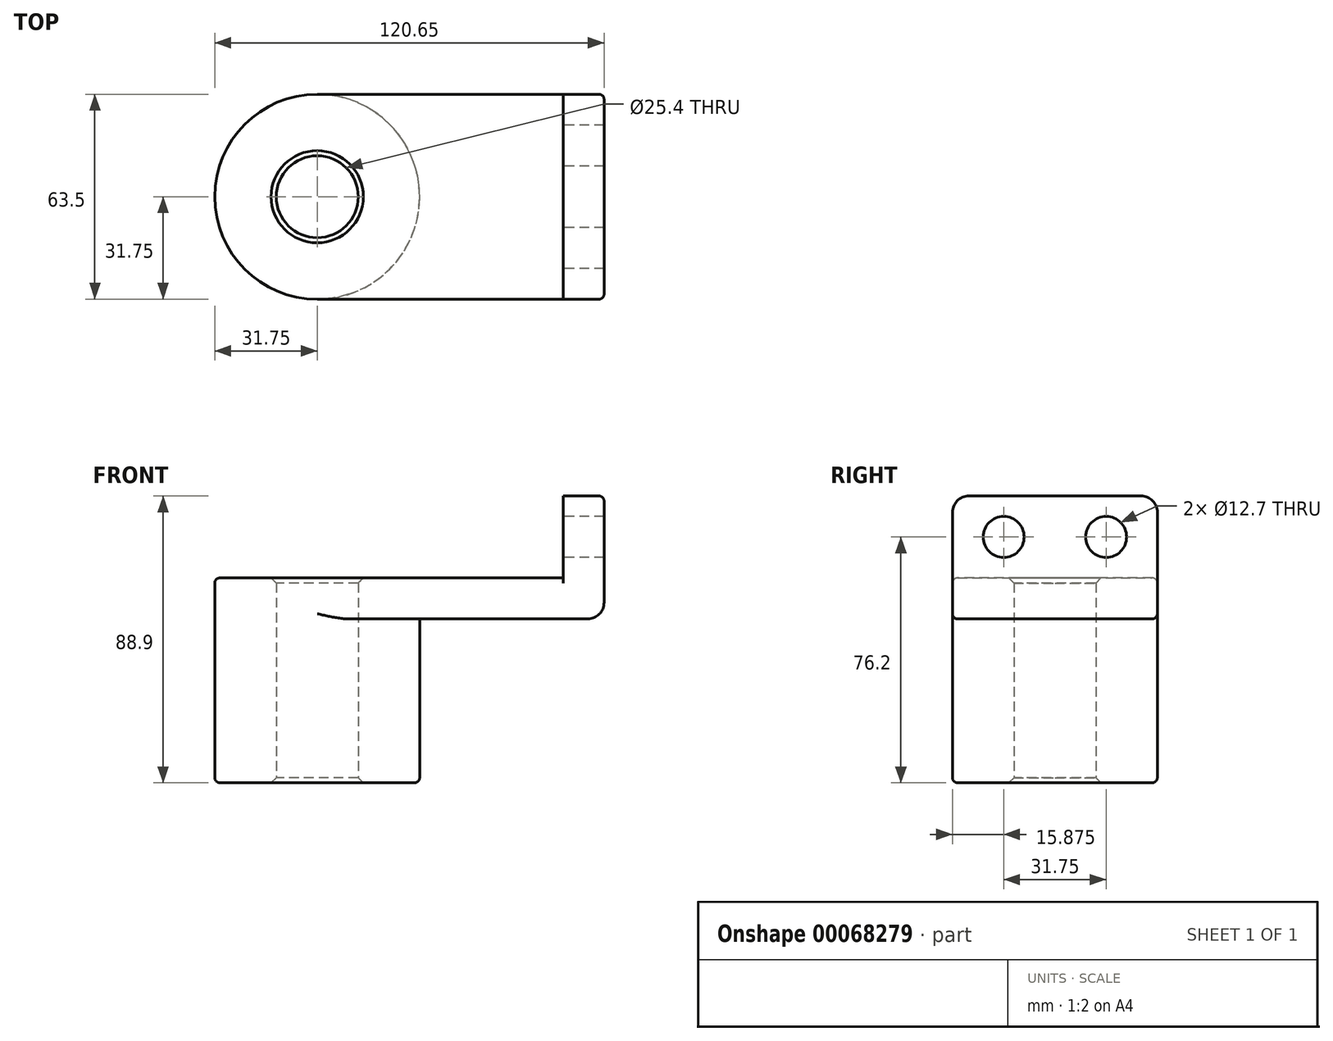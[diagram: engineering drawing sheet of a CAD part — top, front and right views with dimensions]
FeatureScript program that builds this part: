
annotation { "Feature Type Name" : "Feature", "Feature Type Description" : "" }
export const myFeature = defineFeature(function(context is Context, id is Id, definition is map)
    precondition{}
    {
        {
            var Q0;
            Q0=qCreatedBy(makeId("Top.planeOp"),FACE);
            var sketch = newSketch(context, id + "F0", { "sketchPlane" : qUnion([Q0])});
            skLineSegment(sketch, "E0.rect.bottom", {"start": v(38.1, -31.75) * mm, "end": v(-38.1, -31.75) * mm});
            skLineSegment(sketch, "E0.rect.top", {"start": v(38.1, 31.75) * mm, "end": v(-38.1, 31.75) * mm});
            skLineSegment(sketch, "E0.rect.left", {"start": v(38.1, -31.75) * mm, "end": v(38.1, 31.75) * mm});
            skLineSegment(sketch, "E0.rect.right", {"start": v(-38.1, -31.75) * mm, "end": v(-38.1, 31.75) * mm});
            skPoint(sketch, "E0.rect.middle", {"position": v(0, 0) * mm});
            skCircle(sketch, "E1", {"center": v(-38.1, 0) * mm, "radius": 31.75 * mm});
            skCircle(sketch, "E2", {"center": v(-38.1, 0) * mm, "radius": 12.7 * mm});
            skSolve(sketch);
        }
        {
            var Q0;
            {var subQ0=sQuery(id+"F0.wireOp",EDGE,"E0.rect.bottom");Q0=makeQuery(id+"F0.imprint","IMPRINT",FACE,{"disambiguationData":[TD([[makeQuery(id+"F0.imprint","IMPRINT",EDGE,{"derivedFrom":subQ0}),-1.0]])]});}
            var Q1;
            {var subQ1=sQuery(id+"F0.wireOp",EDGE,"E0.rect.right");var subQ3=sQuery(id+"F0.wireOp",EDGE,"E2");var subQ4=makeQuery(id+"F0.imprint","INTERSECT",VERTEX,{"disambiguationData":[OD(0.0)],"derivedFrom":[subQ1,subQ3]});Q1=makeQuery(id+"F0.imprint","IMPRINT",FACE,{"disambiguationData":[TD([[makeQuery(id+"F0.imprint","IMPRINT",EDGE,{"disambiguationData":[TD([[subQ4,-1.0]])],"derivedFrom":subQ3}),-1.0]])]});}
            var Q2;
            {var subQ1=sQuery(id+"F0.wireOp",EDGE,"E0.rect.right");var subQ3=sQuery(id+"F0.wireOp",EDGE,"E2");var subQ4=makeQuery(id+"F0.imprint","INTERSECT",VERTEX,{"disambiguationData":[OD(0.0)],"derivedFrom":[subQ1,subQ3]});Q2=makeQuery(id+"F0.imprint","IMPRINT",FACE,{"disambiguationData":[TD([[makeQuery(id+"F0.imprint","IMPRINT",EDGE,{"disambiguationData":[TD([[subQ4,1.0]])],"derivedFrom":subQ3}),-1.0]])]});}
            extrude(context, id + "F1", {"entities" : qUnion([Q0, Q1, Q2]), "depth" : 12.7 * mm});
        }
        {
            var Q0;
            {var subQ1=sQuery(id+"F0.wireOp",EDGE,"E0.rect.right");var subQ3=sQuery(id+"F0.wireOp",EDGE,"E2");var subQ4=makeQuery(id+"F0.imprint","INTERSECT",VERTEX,{"disambiguationData":[OD(0.0)],"derivedFrom":[subQ1,subQ3]});Q0=makeQuery(id+"F0.imprint","IMPRINT",FACE,{"disambiguationData":[TD([[makeQuery(id+"F0.imprint","IMPRINT",EDGE,{"disambiguationData":[TD([[subQ4,1.0]])],"derivedFrom":subQ3}),-1.0]])]});}
            var Q1;
            {var subQ1=sQuery(id+"F0.wireOp",EDGE,"E0.rect.right");var subQ3=sQuery(id+"F0.wireOp",EDGE,"E2");var subQ4=makeQuery(id+"F0.imprint","INTERSECT",VERTEX,{"disambiguationData":[OD(0.0)],"derivedFrom":[subQ1,subQ3]});Q1=makeQuery(id+"F0.imprint","IMPRINT",FACE,{"disambiguationData":[TD([[makeQuery(id+"F0.imprint","IMPRINT",EDGE,{"disambiguationData":[TD([[subQ4,-1.0]])],"derivedFrom":subQ3}),-1.0]])]});}
            extrude(context, id + "F2", {"entities" : qUnion([Q0, Q1]), "operationType" : NewBodyOperationType.ADD, "oppositeDirection" : true, "depth" : 50.8 * mm});
        }
        {
            var Q0;
            Q0=makeQuery(id+"F1.opExtrude","SWEPT_FACE",FACE,{"disambiguationData":[OSD([sQuery(id+"F0.wireOp",EDGE,"E0.rect.left")])]});
            var sketch = newSketch(context, id + "F3", { "sketchPlane" : qUnion([Q0])});
            skLineSegment(sketch, "E3.bottom", {"start": v(31.75, 0) * mm, "end": v(-31.75, 0) * mm});
            skLineSegment(sketch, "E3.top", {"start": v(31.75, 38.1) * mm, "end": v(-31.75, 38.1) * mm});
            skLineSegment(sketch, "E3.left", {"start": v(31.75, 0) * mm, "end": v(31.75, 38.1) * mm});
            skLineSegment(sketch, "E3.right", {"start": v(-31.75, 0) * mm, "end": v(-31.75, 38.1) * mm});
            skLineSegment(sketch, "E4", {"start": v(0, 12.7) * mm, "end": v(0, 38.1) * mm, "construction": true});
            skCircle(sketch, "E5", {"center": v(15.88, 25.4) * mm, "radius": 6.35 * mm});
            skCircle(sketch, "E6.MirrorC", {"center": v(-15.88, 25.4) * mm, "radius": 6.35 * mm});
            skSolve(sketch);
        }
        {
            var Q0;
            {var subQ2=sQuery(id+"F3.wireOp",EDGE,"E3.top");Q0=makeQuery(id+"F3.imprint","IMPRINT",FACE,{"disambiguationData":[TD([[makeQuery(id+"F3.imprint","IMPRINT",EDGE,{"derivedFrom":subQ2}),1.0]])]});}
            var Q1;
            {var subQ0=sQuery(id+"F3.wireOp",EDGE,"E3.bottom");Q1=makeQuery(id+"F3.imprint","IMPRINT",FACE,{"disambiguationData":[TD([[makeQuery(id+"F3.imprint","IMPRINT",EDGE,{"derivedFrom":subQ0}),1.0]])]});}
            extrude(context, id + "F4", {"entities" : qUnion([Q0, Q1]), "operationType" : NewBodyOperationType.ADD, "depth" : 12.7 * mm});
        }
        {
            var Q0;
            Q0=makeQuery(id+"F2.opExtrude","CAP_EDGE",EDGE,{"disambiguationData":[OSD([sQuery(id+"F0.wireOp",EDGE,"E1")])],"isStart":true});
            var Q1;
            Q1=makeQuery(id+"F4.opExtrude","SWEPT_EDGE",EDGE,{"disambiguationData":[OSD([sQuery(id+"F3.wireOp",EDGE,"E3.top"),sQuery(id+"F3.wireOp",EDGE,"E3.left")])]});
            var Q2;
            Q2=makeQuery(id+"F4.opExtrude","SWEPT_EDGE",EDGE,{"disambiguationData":[OSD([sQuery(id+"F3.wireOp",EDGE,"E3.top"),sQuery(id+"F3.wireOp",EDGE,"E3.right")])]});
            var Q3;
            Q3=makeQuery(id+"F4.opExtrude","CAP_EDGE",EDGE,{"disambiguationData":[OSD([sQuery(id+"F3.wireOp",EDGE,"E3.bottom")])],"isStart":false});
            var Q4;
            Q4=makeQuery(id+"F1.opExtrude","CAP_EDGE",EDGE,{"disambiguationData":[OSD([sQuery(id+"F0.wireOp",EDGE,"E0.rect.left")])],"isStart":false});
            fillet(context, id + "F5", {"entities" : qUnion([Q0, Q1, Q2, Q3, Q4]), "radius" : 5.08 * mm, "tangentPropagation" : true, "allowEdgeOverflow" : false});
        }
        {
            var Q0;
            Q0=makeQuery(id+"F1.opExtrude","CAP_EDGE",EDGE,{"disambiguationData":[OSD([sQuery(id+"F0.wireOp",EDGE,"E0.rect.bottom")])],"isStart":false});
            var Q1;
            Q1=makeQuery(id+"F4.boolean.opBoolean","MERGE",EDGE,{"derivedFrom":[makeQuery(id+"F1.opExtrude","CAP_EDGE",EDGE,{"disambiguationData":[OSD([sQuery(id+"F0.wireOp",EDGE,"E0.rect.bottom")])],"isStart":true}),makeQuery(id+"F4.opExtrude","SWEPT_EDGE",EDGE,{"disambiguationData":[OSD([sQuery(id+"F3.wireOp",EDGE,"E3.bottom"),sQuery(id+"F3.wireOp",EDGE,"E3.right")])]})]});
            var Q2;
            Q2=makeQuery(id+"F2.opExtrude","CAP_EDGE",EDGE,{"disambiguationData":[OSD([sQuery(id+"F0.wireOp",EDGE,"E1")])],"isStart":false});
            fillet(context, id + "F6", {"entities" : qUnion([Q0, Q1, Q2]), "radius" : 1.59 * mm, "tangentPropagation" : true, "allowEdgeOverflow" : false});
        }
        {
            var Q0;
            {var subQ0=sQuery(id+"F0.wireOp",EDGE,"E2");Q0=makeQuery(id+"F2.boolean.opBoolean","MERGE",FACE,{"derivedFrom":[makeQuery(id+"F1.opExtrude","SWEPT_FACE",FACE,{"disambiguationData":[OSD([subQ0])]}),makeQuery(id+"F2.opExtrude","SWEPT_FACE",FACE,{"disambiguationData":[OSD([subQ0])]})]});}
            chamfer(context, id + "F7", {"entities" : qUnion([Q0]), "width" : 1.59 * mm, "tangentPropagation" : true});
        }
    });
